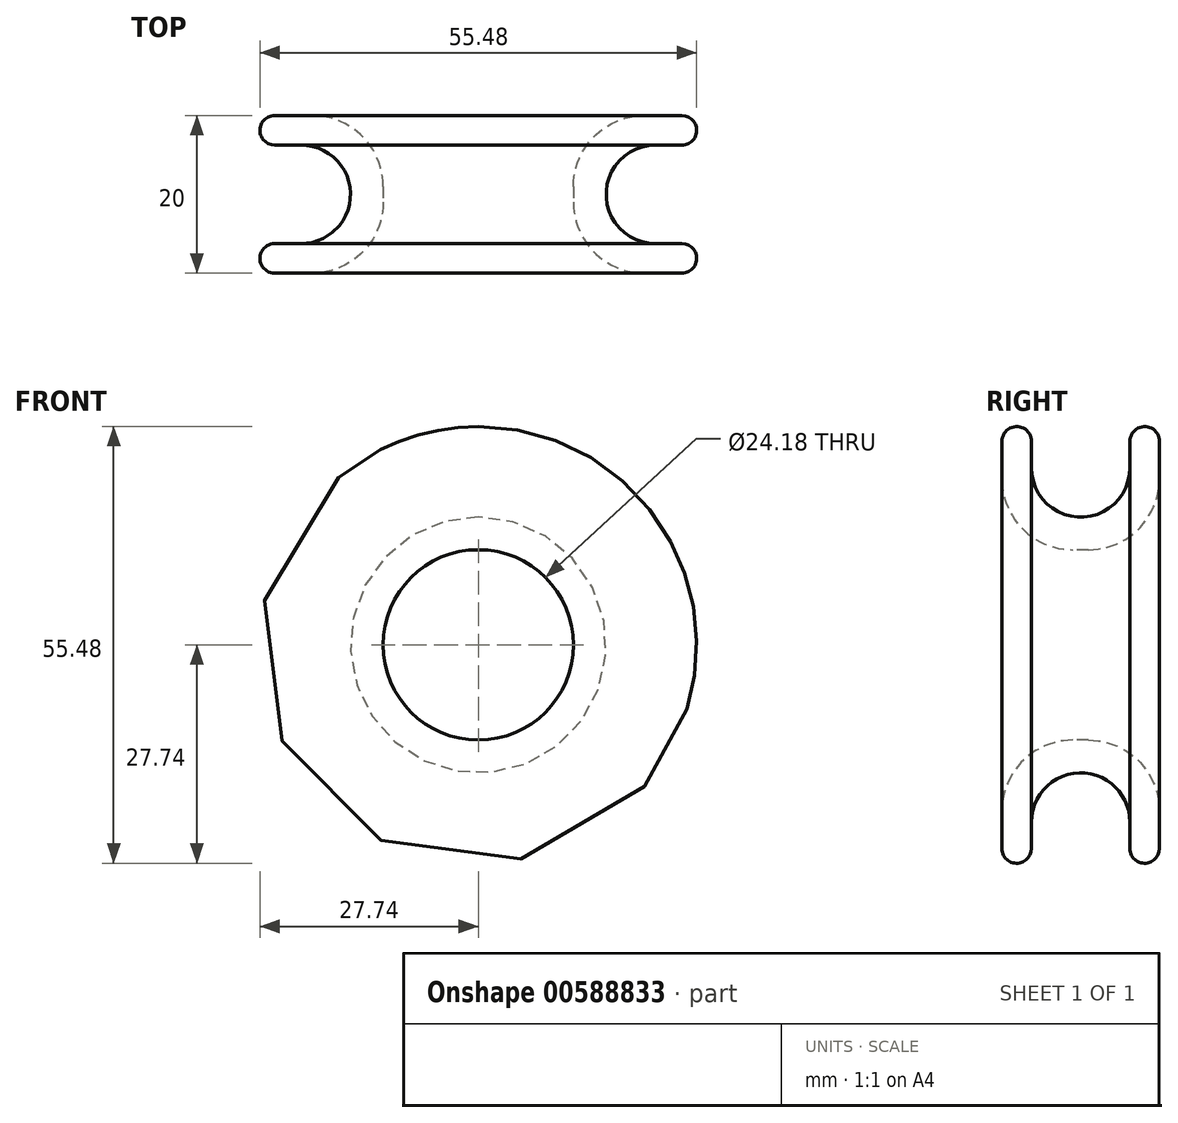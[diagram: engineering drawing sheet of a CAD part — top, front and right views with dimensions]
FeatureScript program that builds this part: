
annotation { "Feature Type Name" : "Feature", "Feature Type Description" : "" }
export const myFeature = defineFeature(function(context is Context, id is Id, definition is map)
    precondition{}
    {
        {
            var Q0;
            Q0=qCreatedBy(makeId("Front.planeOp"),FACE);
            var sketch = newSketch(context, id + "F0", { "sketchPlane" : qUnion([Q0])});
            skCircle(sketch, "E0", {"center": v(0, 0) * mm, "radius": 22.5 * mm});
            skSolve(sketch);
        }
        {
            var Q0;
            Q0=qCreatedBy(makeId("Right.planeOp"),FACE);
            var sketch = newSketch(context, id + "F1", { "sketchPlane" : qUnion([Q0])});
            skCircle(sketch, "E1", {"center": v(0, 22.5) * mm, "radius": 4.76 * mm, "construction": true});
            skLineSegment(sketch, "E2.0", {"start": v(0, -22.5) * mm, "end": v(0, 22.5) * mm, "construction": true});
            skArc(sketch, "E3", {"start": v(-6.26, 22.5) * mm, "mid": v(0, 16.24) * mm, "end": v(6.26, 22.5) * mm});
            skLineSegment(sketch, "E4", {"start": v(-6.26, 22.5) * mm, "end": v(-6.26, 25.87) * mm});
            skLineSegment(sketch, "E5", {"start": v(-10, 25.87) * mm, "end": v(-10, 21.1) * mm});
            skLineSegment(sketch, "E6", {"start": v(-1, 12.1) * mm, "end": v(0, 12.1) * mm});
            skLineSegment(sketch, "E7.MirrorCS", {"start": v(1, 12.1) * mm, "end": v(0, 12.1) * mm});
            skLineSegment(sketch, "E8.MirrorCS", {"start": v(10, 25.87) * mm, "end": v(10, 21.1) * mm});
            skLineSegment(sketch, "E9.MirrorCS", {"start": v(6.26, 22.5) * mm, "end": v(6.26, 25.87) * mm});
            skArc(sketch, "E10", {"start": v(-10, 25.87) * mm, "mid": v(-8.13, 27.74) * mm, "end": v(-6.26, 25.87) * mm});
            skArc(sketch, "E11", {"start": v(6.26, 25.87) * mm, "mid": v(8.13, 27.74) * mm, "end": v(10, 25.87) * mm});
            skPoint(sketch, "E12.visualSharp", {"position": v(-3.8, 12.1) * mm});
            skLineSegment(sketch, "E13", {"start": v(-10, 14.24) * mm, "end": v(10, 14.24) * mm, "construction": true});
            skPoint(sketch, "E14.visualSharp", {"position": v(-10, 14.24) * mm});
            skPoint(sketch, "E15.visualSharp", {"position": v(10, 14.24) * mm});
            skArc(sketch, "E16", {"start": v(-10, 21.1) * mm, "mid": v(-7.36, 14.73) * mm, "end": v(-1, 12.1) * mm});
            skArc(sketch, "E17", {"start": v(10, 21.1) * mm, "mid": v(7.36, 14.73) * mm, "end": v(1, 12.1) * mm});
            skSolve(sketch);
        }
        {
            var Q0;
            Q0=makeQuery(id+"F1.imprint","IMPRINT",FACE,{"disambiguationData":[TD([[makeQuery(id+"F1.imprint","IMPRINT",EDGE,{"derivedFrom":sQuery(id+"F1.wireOp",EDGE,"E3")}),-1.0]])]});
            var Q1;
            Q1=sQuery(id+"F0.wireOp",EDGE,"E0");
            sweep(context, id + "F2", {"profiles" : qUnion([Q0]), "path" : qUnion([Q1])});
        }
    });
